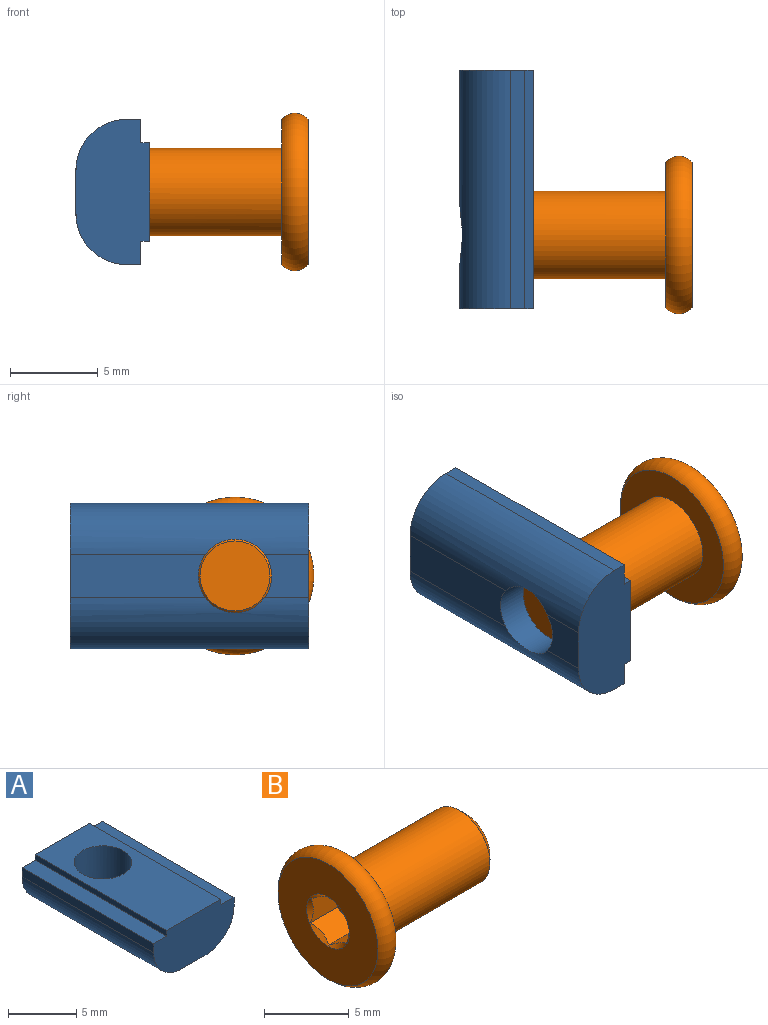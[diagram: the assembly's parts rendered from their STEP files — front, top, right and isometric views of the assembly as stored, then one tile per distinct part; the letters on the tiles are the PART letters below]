
ASSEMBLY  parts=2 mates=1
PART A: 14 faces, bbox 8.3x13.6x4.2 mm
  f0: cylinder r=2.1mm len=4.2mm, axis (0,0,1), area 55.4mm2, adj f1,f5,f6,f7,f11
  f1: plane 2.51x2.5mm, normal (0,0,-1), area 5.6mm2, adj f0,f5,f7,f13
  f2: plane 13.6x0.5mm, normal (-1,0,0), area 6.8mm2, adj f3,f11,f12,f13
  f3: plane 13.6x1.35mm, normal (0,0,1), area 18.4mm2, adj f2,f4,f12,f13
  f4: plane 13.6x0.8mm, normal (-1,0,0), area 10.9mm2, adj f3,f5,f12,f13
  f5: cylinder r=2.9mm len=13.6mm, axis (0,1,0), area 59.9mm2, adj f0,f1,f4,f6,f12,f13
  f6: plane 7.71x2.5mm, normal (0,0,-1), area 18.6mm2, adj f0,f5,f7,f12
  f7: cylinder r=2.9mm len=13.6mm, axis (0,1,0), area 59.9mm2, adj f0,f1,f6,f8,f12,f13
  f8: plane 13.6x0.8mm, normal (1,0,0), area 10.9mm2, adj f7,f9,f12,f13
  f9: plane 13.6x1.35mm, normal (0,0,1), area 18.4mm2, adj f8,f10,f12,f13
  f10: plane 13.6x0.5mm, normal (1,0,0), area 6.8mm2, adj f9,f11,f12,f13
  f11: plane 13.6x5.6mm, normal (0,0,1), area 62.3mm2, adj f0,f2,f10,f12,f13
  f12: plane 8.3x4.2mm, normal (0,-1,0), area 29.9mm2, adj f2,f3,f4,f5,f6,f7,f8,f9
  f13: plane 8.3x4.2mm, normal (0,1,0), area 29.9mm2, adj f1,f2,f3,f4,f5,f7,f8,f9
PART B: 14 faces, bbox 11.8x9.7x9.7 mm
  f0: cone r=1.78mm half-angle=45deg, axis (-1,0,0), area 3.1mm2, adj f5,f8,f9,f10,f11,f12,f13
  f1: torus R=3.5mm, axis (1,0,0), area 46.7mm2, adj f5,f6
  f2: cone r=2mm half-angle=45deg, axis (-1,0,0), area 10mm2, adj f3,f4
  f3: cylinder r=2.5mm len=9.5mm, axis (1,0,0), area 149.2mm2, adj f2,f6
  f4: plane 4x4mm, normal (1,0,0), area 12.6mm2, adj f2
  f5: plane 8.32x8.32mm, normal (-1,0,0), area 44.4mm2, adj f0,f1
  f6: plane 8.32x8.32mm, normal (1,0,0), area 34.8mm2, adj f1,f3
  f7: plane 3.46x3mm, normal (-1,0,0), area 7.8mm2, adj f8,f9,f10,f11,f12,f13
  f8: plane 2.25x1.5mm, normal (0,-0.5,-0.87), area 3.6mm2, adj f0,f7,f9,f13
  f9: plane 2.25x1.73mm, normal (0,-1,0), area 3.6mm2, adj f0,f7,f8,f10
  f10: plane 2.25x1.5mm, normal (0,-0.5,0.87), area 3.6mm2, adj f0,f7,f9,f11
  f11: plane 2.25x1.5mm, normal (0,0.5,0.87), area 3.6mm2, adj f0,f7,f10,f12
  f12: plane 2.25x1.73mm, normal (0,1,0), area 3.6mm2, adj f0,f7,f11,f13
  f13: plane 2.25x1.5mm, normal (0,0.5,-0.87), area 3.6mm2, adj f0,f7,f8,f12
PLACE A rot(axis=(-0.71,0,-0.71),180deg) t=(11.24,-12.19,-2.91)mm
PLACE B rot(axis=(0,-0.71,-0.71),180deg) t=(10.79,-7.99,-2.91)mm
MATE cylindrical B.f2 <-> A.f0  axis (-1,0,0) through (14.04,-7.99,-2.91)mm
